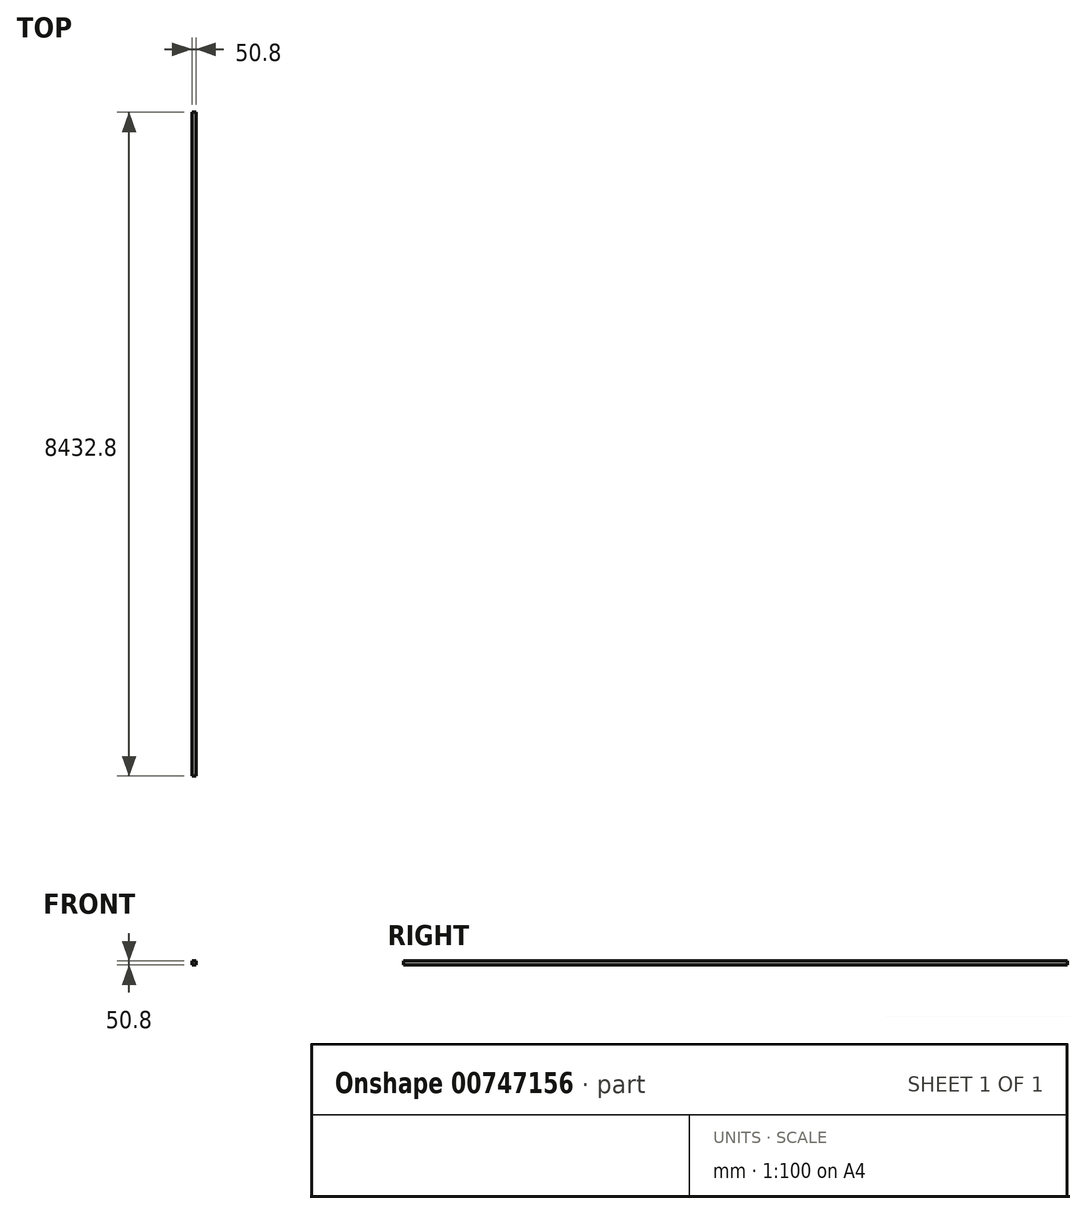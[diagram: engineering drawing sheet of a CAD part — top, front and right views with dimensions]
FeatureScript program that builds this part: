
annotation { "Feature Type Name" : "Feature", "Feature Type Description" : "" }
export const myFeature = defineFeature(function(context is Context, id is Id, definition is map)
    precondition{}
    {
        {
            var Q0;
            Q0=qCreatedBy(makeId("Front.planeOp"),FACE);
            var sketch = newSketch(context, id + "F0", { "sketchPlane" : qUnion([Q0])});
            skLineSegment(sketch, "E0.bottom", {"start": v(-81, 50.29) * mm, "end": v(-30.2, 50.29) * mm});
            skLineSegment(sketch, "E0.top", {"start": v(-81, -0.51) * mm, "end": v(-30.2, -0.51) * mm});
            skLineSegment(sketch, "E0.left", {"start": v(-81, 50.29) * mm, "end": v(-81, -0.51) * mm});
            skLineSegment(sketch, "E0.right", {"start": v(-30.2, 50.29) * mm, "end": v(-30.2, -0.51) * mm});
            skSolve(sketch);
        }
        {
            var Q0;
            Q0 = qSketchRegion(id + "F0", true);
            extrude(context, id + "F1", {"entities" : qUnion([Q0]), "depth" : 8432.8 * mm, "offsetDistance" : 25.4 * mm});
        }
    });
